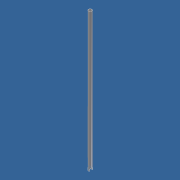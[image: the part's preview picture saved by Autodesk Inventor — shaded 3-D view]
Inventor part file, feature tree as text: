
AUTODESK INVENTOR PART (.ipt)
format: ipt  version: unknown  size: 176,128 bytes
history: native  units: mm
features: extrude x2, sketch x2
ambient origin geometry x8: Origin, YZ Plane, XZ Plane, XY Plane, X Axis, Y Axis, Z Axis, Center Point
bodies: Solido1 (feature_tree)
feature tree (4):
  extrude  "Estrusione1"  Depth=25.0mm
  extrude  "Estrusione2"  Depth=1.0mm
  sketch  "Schizzo1"
  sketch  "Schizzo2"
